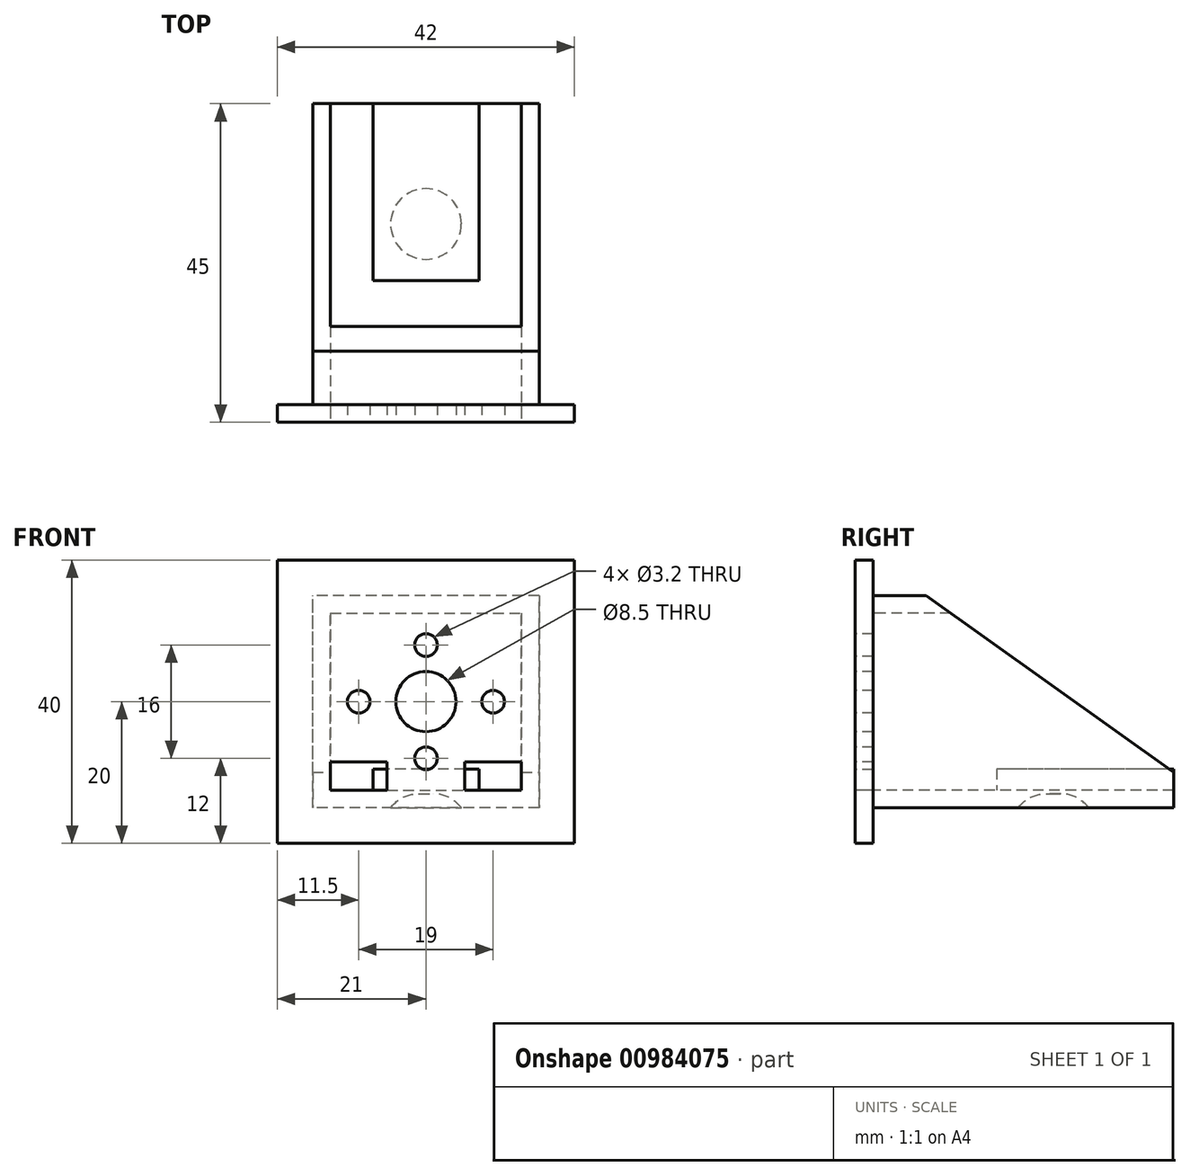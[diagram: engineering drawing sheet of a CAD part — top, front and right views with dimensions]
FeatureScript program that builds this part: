
annotation { "Feature Type Name" : "Feature", "Feature Type Description" : "" }
export const myFeature = defineFeature(function(context is Context, id is Id, definition is map)
    precondition{}
    {
        {
            var Q0;
            Q0=qCreatedBy(makeId("Front.planeOp"),FACE);
            var sketch = newSketch(context, id + "F0", { "sketchPlane" : qUnion([Q0])});
            skLineSegment(sketch, "E0.bottom", {"start": v(-16, 15) * mm, "end": v(16, 15) * mm});
            skLineSegment(sketch, "E0.top", {"start": v(-16, -15) * mm, "end": v(16, -15) * mm});
            skLineSegment(sketch, "E0.left", {"start": v(-16, 15) * mm, "end": v(-16, -15) * mm});
            skLineSegment(sketch, "E0.right", {"start": v(16, 15) * mm, "end": v(16, -15) * mm});
            skPoint(sketch, "E0.middle", {"position": v(0, 0) * mm});
            skSolve(sketch);
        }
        {
            var Q0;
            Q0 = qSketchRegion(id + "F0", true);
            extrude(context, id + "F1", {"entities" : qUnion([Q0]), "oppositeDirection" : true, "depth" : 45 * mm, "offsetDistance" : 25 * mm});
        }
        {
            var Q0;
            Q0=makeQuery(id+"F1.opExtrude","CAP_FACE",FACE,{"disambiguationData":[OSD([sQuery(id+"F0.wireOp",EDGE,"E0.bottom"),sQuery(id+"F0.wireOp",EDGE,"E0.top"),sQuery(id+"F0.wireOp",EDGE,"E0.left"),sQuery(id+"F0.wireOp",EDGE,"E0.right")])],"isStart":false});
            shell(context, id + "F2", {"entities" : qUnion([Q0]), "thickness" : 2.5 * mm});
        }
        {
            var Q0;
            Q0=makeQuery(id+"F1.opExtrude","SWEPT_FACE",FACE,{"disambiguationData":[OSD([sQuery(id+"F0.wireOp",EDGE,"E0.right")])]});
            var sketch = newSketch(context, id + "F3", { "sketchPlane" : qUnion([Q0])});
            skLineSegment(sketch, "E1", {"start": v(10, 15) * mm, "end": v(45, -10) * mm});
            skLineSegment(sketch, "E2", {"start": v(45, -10) * mm, "end": v(45, 15) * mm});
            skLineSegment(sketch, "E3", {"start": v(45, 15) * mm, "end": v(10, 15) * mm});
            skSolve(sketch);
        }
        {
            var Q0;
            Q0 = qSketchRegion(id + "F3", true);
            extrude(context, id + "F4", {"entities" : qUnion([Q0]), "operationType" : NewBodyOperationType.REMOVE, "endBound" : BoundingType.THROUGH_ALL, "oppositeDirection" : true, "depth" : 25 * mm, "offsetDistance" : 25 * mm});
        }
        {
            var Q0;
            Q0=makeQuery(id+"F1.opExtrude","CAP_FACE",FACE,{"disambiguationData":[OSD([sQuery(id+"F0.wireOp",EDGE,"E0.bottom"),sQuery(id+"F0.wireOp",EDGE,"E0.top"),sQuery(id+"F0.wireOp",EDGE,"E0.left"),sQuery(id+"F0.wireOp",EDGE,"E0.right")])],"isStart":true});
            var sketch = newSketch(context, id + "F5", { "sketchPlane" : qUnion([Q0])});
            skLineSegment(sketch, "E4.bottom", {"start": v(21, 20) * mm, "end": v(-21, 20) * mm});
            skLineSegment(sketch, "E4.top", {"start": v(21, -20) * mm, "end": v(-21, -20) * mm});
            skLineSegment(sketch, "E4.left", {"start": v(21, 20) * mm, "end": v(21, -20) * mm});
            skLineSegment(sketch, "E4.right", {"start": v(-21, 20) * mm, "end": v(-21, -20) * mm});
            skPoint(sketch, "E4.middle", {"position": v(0, 0) * mm});
            skSolve(sketch);
        }
        {
            var Q0;
            Q0 = qSketchRegion(id + "F5", true);
            extrude(context, id + "F6", {"entities" : qUnion([Q0]), "operationType" : NewBodyOperationType.ADD, "oppositeDirection" : true, "depth" : 2.5 * mm, "offsetDistance" : 25 * mm});
        }
        {
            var Q0;
            Q0=makeQuery(id+"F6.boolean.opBoolean","MERGE",FACE,{"derivedFrom":[makeQuery(id+"F1.opExtrude","CAP_FACE",FACE,{"disambiguationData":[OSD([sQuery(id+"F0.wireOp",EDGE,"E0.bottom"),sQuery(id+"F0.wireOp",EDGE,"E0.top"),sQuery(id+"F0.wireOp",EDGE,"E0.left"),sQuery(id+"F0.wireOp",EDGE,"E0.right")])],"isStart":true}),makeQuery(id+"F6.opExtrude","CAP_FACE",FACE,{"disambiguationData":[OSD([sQuery(id+"F5.wireOp",EDGE,"E4.bottom"),sQuery(id+"F5.wireOp",EDGE,"E4.top"),sQuery(id+"F5.wireOp",EDGE,"E4.left"),sQuery(id+"F5.wireOp",EDGE,"E4.right")])],"isStart":true})]});
            var sketch = newSketch(context, id + "F7", { "sketchPlane" : qUnion([Q0])});
            skCircle(sketch, "E5", {"center": v(0, 0) * mm, "radius": 8 * mm, "construction": true});
            skCircle(sketch, "E6", {"center": v(0, 0) * mm, "radius": 9.5 * mm, "construction": true});
            skCircle(sketch, "E7", {"center": v(9.5, 0) * mm, "radius": 1.6 * mm});
            skCircle(sketch, "E8", {"center": v(-9.5, 0) * mm, "radius": 1.6 * mm});
            skCircle(sketch, "E9", {"center": v(0, -8) * mm, "radius": 1.6 * mm});
            skCircle(sketch, "E10", {"center": v(0, 8) * mm, "radius": 1.6 * mm});
            skCircle(sketch, "E11", {"center": v(0, 0) * mm, "radius": 4.25 * mm});
            skLineSegment(sketch, "E12.bottom", {"start": v(5.5, -8.5) * mm, "end": v(13.5, -8.5) * mm});
            skLineSegment(sketch, "E12.top", {"start": v(5.5, -12.5) * mm, "end": v(13.5, -12.5) * mm});
            skLineSegment(sketch, "E12.left", {"start": v(5.5, -8.5) * mm, "end": v(5.5, -12.5) * mm});
            skLineSegment(sketch, "E12.right", {"start": v(13.5, -8.5) * mm, "end": v(13.5, -12.5) * mm});
            skLineSegment(sketch, "E13.bottom", {"start": v(-5.5, -8.5) * mm, "end": v(-13.5, -8.5) * mm});
            skLineSegment(sketch, "E13.top", {"start": v(-5.5, -12.5) * mm, "end": v(-13.5, -12.5) * mm});
            skLineSegment(sketch, "E13.left", {"start": v(-5.5, -8.5) * mm, "end": v(-5.5, -12.5) * mm});
            skLineSegment(sketch, "E13.right", {"start": v(-13.5, -8.5) * mm, "end": v(-13.5, -12.5) * mm});
            skSolve(sketch);
        }
        {
            var Q0;
            Q0 = qSketchRegion(id + "F7", true);
            extrude(context, id + "F8", {"entities" : qUnion([Q0]), "operationType" : NewBodyOperationType.REMOVE, "endBound" : BoundingType.THROUGH_ALL, "oppositeDirection" : true, "depth" : 25 * mm, "offsetDistance" : 25 * mm});
        }
        {
            var Q0;
            Q0=makeQuery(id+"F8.boolean.opBoolean","MERGE",FACE,{"derivedFrom":[makeQuery(id+"F2.opShell","OFFSET_FACE",FACE,{"disambiguationData":[OSD([sQuery(id+"F0.wireOp",EDGE,"E0.top")])]})],"fromTools":[makeQuery(id+"F8.opExtrude","SWEPT_FACE",FACE,{"disambiguationData":[OSD([sQuery(id+"F7.wireOp",EDGE,"E12.top")])]})]});
            var sketch = newSketch(context, id + "F9", { "sketchPlane" : qUnion([Q0])});
            skLineSegment(sketch, "E14.bottom", {"start": v(7.5, 45) * mm, "end": v(-7.5, 45) * mm});
            skLineSegment(sketch, "E14.top", {"start": v(7.5, 20) * mm, "end": v(-7.5, 20) * mm});
            skLineSegment(sketch, "E14.left", {"start": v(7.5, 45) * mm, "end": v(7.5, 20) * mm});
            skLineSegment(sketch, "E14.right", {"start": v(-7.5, 45) * mm, "end": v(-7.5, 20) * mm});
            skSolve(sketch);
        }
        {
            var Q0;
            Q0 = qSketchRegion(id + "F9", true);
            extrude(context, id + "F10", {"entities" : qUnion([Q0]), "operationType" : NewBodyOperationType.ADD, "depth" : 3 * mm, "offsetDistance" : 25 * mm});
        }
        {
            var Q0;
            Q0=makeQuery(id+"F1.opExtrude","SWEPT_FACE",FACE,{"disambiguationData":[OSD([sQuery(id+"F0.wireOp",EDGE,"E0.top")])]});
            var sketch = newSketch(context, id + "F11", { "sketchPlane" : qUnion([Q0])});
            skCircle(sketch, "E15", {"center": v(0, -28) * mm, "radius": 5 * mm});
            skSolve(sketch);
        }
        {
            var Q0;
            Q0 = qSketchRegion(id + "F11", true);
            extrude(context, id + "F12", {"entities" : qUnion([Q0]), "operationType" : NewBodyOperationType.REMOVE, "oppositeDirection" : true, "depth" : 2 * mm, "offsetDistance" : 25 * mm});
        }
        {
            var Q0;
            Q0=makeQuery(id+"F12.boolean.opBoolean","COPY",EDGE,{"derivedFrom":makeQuery(id+"F12.opExtrude","CAP_EDGE",EDGE,{"disambiguationData":[OSD([sQuery(id+"F11.wireOp",EDGE,"E15")])],"isStart":false})});
            fillet(context, id + "F13", {"entities" : qUnion([Q0]), "radius" : 5 * mm, "tangentPropagation" : true, "allowEdgeOverflow" : false});
        }
    });
